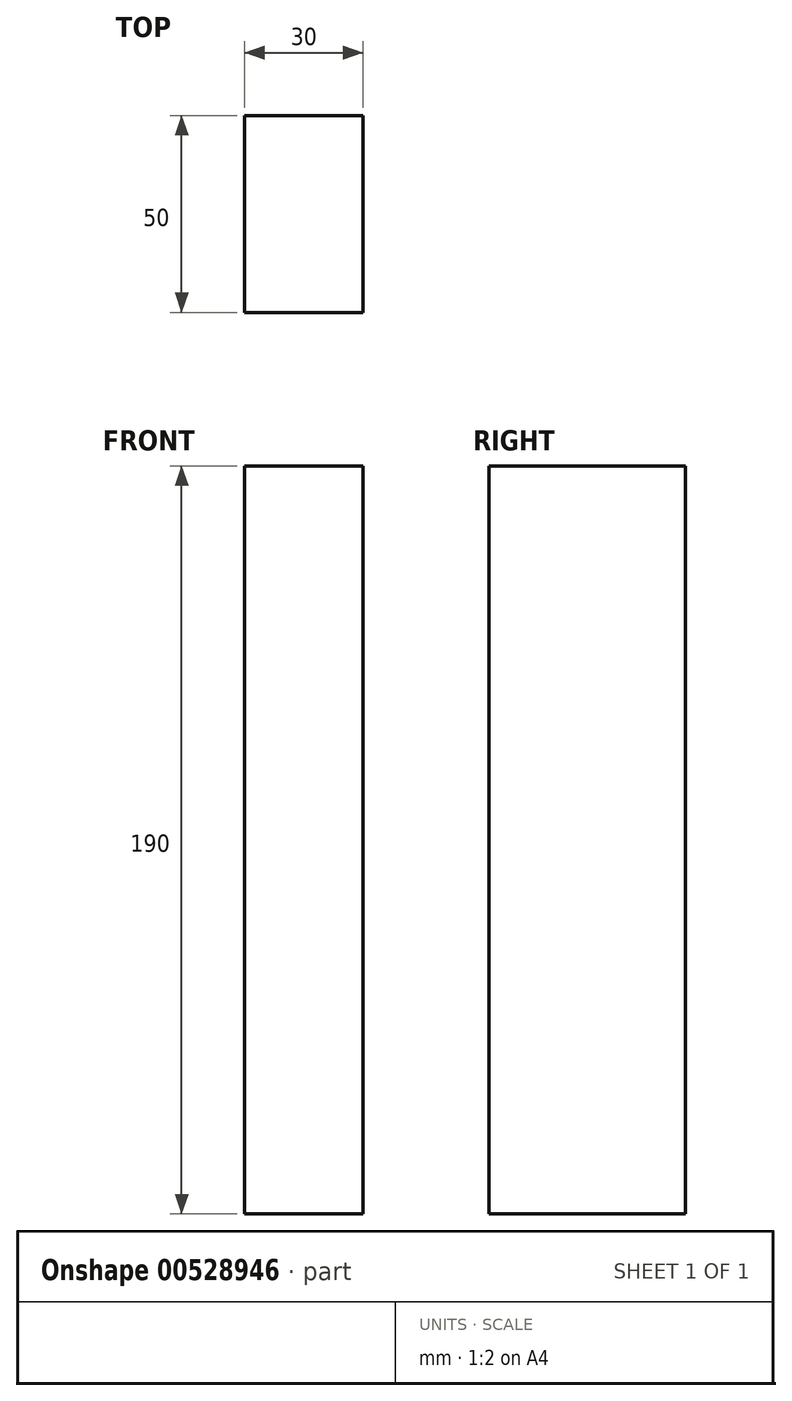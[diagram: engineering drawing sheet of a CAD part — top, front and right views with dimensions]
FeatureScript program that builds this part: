
annotation { "Feature Type Name" : "Feature", "Feature Type Description" : "" }
export const myFeature = defineFeature(function(context is Context, id is Id, definition is map)
    precondition{}
    {
        {
            var Q0;
            Q0=qCreatedBy(makeId("Top.planeOp"),FACE);
            var sketch = newSketch(context, id + "F0", { "sketchPlane" : qUnion([Q0])});
            skLineSegment(sketch, "E0.bottom", {"start": v(15, -25) * mm, "end": v(-15, -25) * mm});
            skLineSegment(sketch, "E0.top", {"start": v(15, 25) * mm, "end": v(-15, 25) * mm});
            skLineSegment(sketch, "E0.left", {"start": v(15, -25) * mm, "end": v(15, 25) * mm});
            skLineSegment(sketch, "E0.right", {"start": v(-15, -25) * mm, "end": v(-15, 25) * mm});
            skPoint(sketch, "E0.middle", {"position": v(0, 0) * mm});
            skSolve(sketch);
        }
        {
            var Q0;
            Q0 = qSketchRegion(id + "F0", true);
            extrude(context, id + "F1", {"entities" : qUnion([Q0]), "depth" : 190 * mm, "offsetDistance" : 25 * mm});
        }
    });
